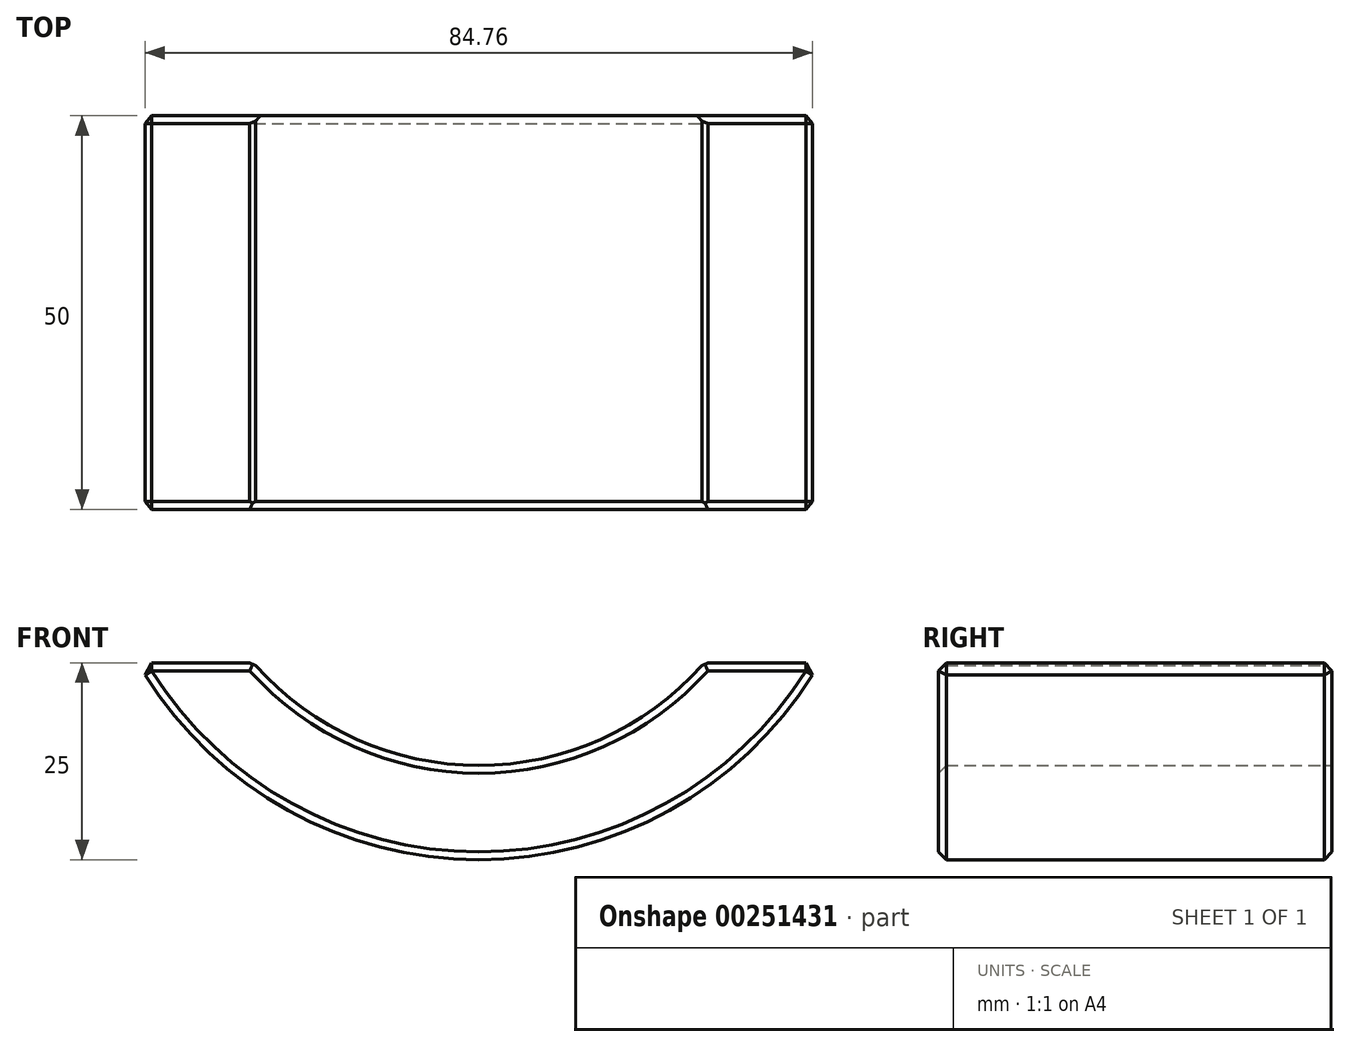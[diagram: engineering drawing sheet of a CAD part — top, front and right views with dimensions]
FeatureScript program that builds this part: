
annotation { "Feature Type Name" : "Feature", "Feature Type Description" : "" }
export const myFeature = defineFeature(function(context is Context, id is Id, definition is map)
    precondition{}
    {
        {
            var Q0;
            Q0=qCreatedBy(makeId("Front.planeOp"),FACE);
            var sketch = newSketch(context, id + "F0", { "sketchPlane" : qUnion([Q0])});
            skCircle(sketch, "E0", {"center": v(0, 0) * mm, "radius": 50 * mm});
            skLineSegment(sketch, "E1", {"start": v(-55.86, -25) * mm, "end": v(60.42, -25) * mm});
            skSolve(sketch);
        }
        {
            var Q0;
            {var subQ0=sQuery(id+"F0.wireOp",EDGE,"E1");var subQ1=sQuery(id+"F0.wireOp",EDGE,"E0");var subQ2=makeQuery(id+"F0.imprint","INTERSECT",VERTEX,{"disambiguationData":[OD(0.0)],"derivedFrom":[subQ1,subQ0]});Q0=makeQuery(id+"F0.imprint","IMPRINT",FACE,{"disambiguationData":[TD([[makeQuery(id+"F0.imprint","IMPRINT",EDGE,{"disambiguationData":[TD([[subQ2,1.0]])],"derivedFrom":subQ1}),1.0]])]});}
            extrude(context, id + "F1", {"entities" : qUnion([Q0]), "depth" : 50 * mm});
        }
        {
            var Q0;
            {var subQ0=sQuery(id+"F0.wireOp",EDGE,"E1");var subQ1=sQuery(id+"F0.wireOp",EDGE,"E0");Q0=makeQuery(id+"F1.opExtrude","SWEPT_EDGE",EDGE,{"disambiguationData":[OSD([subQ1,subQ0]),TDD([makeQuery(id+"F0.imprint","INTERSECT",VERTEX,{"disambiguationData":[OD(1.0)],"derivedFrom":[subQ1,subQ0]})])]});}
            cPlane(context, id + "F2", {"entities" : qUnion([Q0]), "cplaneType" : CPlaneType.LINE_ANGLE, "offset" : 25 * mm, "angle" : 90 * degree, "width" : 150 * mm, "height" : 150 * mm});
        }
        {
            var Q0;
            Q0=qCreatedBy(id+"F2.planeOp",FACE);
            var sketch = newSketch(context, id + "F3", { "sketchPlane" : qUnion([Q0])});
            skLineSegment(sketch, "E2.bottom", {"start": v(-42.5, 50.98) * mm, "end": v(-7.5, 50.98) * mm});
            skLineSegment(sketch, "E2.top", {"start": v(-42.5, -15) * mm, "end": v(-7.5, -15) * mm});
            skLineSegment(sketch, "E2.left", {"start": v(-42.5, 50.98) * mm, "end": v(-42.5, -15) * mm});
            skLineSegment(sketch, "E2.right", {"start": v(-7.5, 50.98) * mm, "end": v(-7.5, -15) * mm});
            skLineSegment(sketch, "E3", {"start": v(-50, 50) * mm, "end": v(0, 50) * mm});
            skLineSegment(sketch, "E4", {"start": v(-50, 50) * mm, "end": v(0, 50) * mm, "construction": true});
            skSolve(sketch);
        }
        {
            var Q0;
            Q0 = qSketchRegion(id + "F3", true);
            extrude(context, id + "F4", {"entities" : qUnion([Q0]), "operationType" : NewBodyOperationType.REMOVE, "oppositeDirection" : true, "depth" : 123.6 * mm, "hasSecondDirection" : true, "secondDirectionOppositeDirection" : false, "secondDirectionDepth" : 25 * mm});
        }
        {
            var Q0;
            Q0=makeQuery(id+"F1.opExtrude","CAP_EDGE",EDGE,{"disambiguationData":[OSD([sQuery(id+"F0.wireOp",EDGE,"E0")])],"isStart":true});
            var Q1;
            Q1=makeQuery(id+"F4.boolean.opBoolean","INTERSECT",EDGE,{"derivedFrom":[makeQuery(id+"F1.opExtrude","SWEPT_FACE",FACE,{"disambiguationData":[OSD([sQuery(id+"F0.wireOp",EDGE,"E0")])]}),makeQuery(id+"F4.opExtrude","SWEPT_FACE",FACE,{"disambiguationData":[OSD([sQuery(id+"F3.wireOp",EDGE,"E2.right")])]})]});
            var Q2;
            Q2=makeQuery(id+"F4.boolean.opBoolean","INTERSECT",EDGE,{"derivedFrom":[makeQuery(id+"F1.opExtrude","SWEPT_FACE",FACE,{"disambiguationData":[OSD([sQuery(id+"F0.wireOp",EDGE,"E0")])]}),makeQuery(id+"F4.opExtrude","SWEPT_FACE",FACE,{"disambiguationData":[OSD([sQuery(id+"F3.wireOp",EDGE,"E2.left")])]})]});
            var Q3;
            Q3=makeQuery(id+"F1.opExtrude","CAP_EDGE",EDGE,{"disambiguationData":[OSD([sQuery(id+"F0.wireOp",EDGE,"E0")])],"isStart":false});
            var Q4;
            Q4=makeQuery(id+"F4.boolean.opBoolean","INTERSECT",EDGE,{"disambiguationData":[OD(1.0)],"derivedFrom":[makeQuery(id+"F1.opExtrude","SWEPT_FACE",FACE,{"disambiguationData":[OSD([sQuery(id+"F0.wireOp",EDGE,"E0")])]}),makeQuery(id+"F4.opExtrude","SWEPT_FACE",FACE,{"disambiguationData":[OSD([sQuery(id+"F3.wireOp",EDGE,"E2.top")])]})]});
            var Q5;
            {var subQ0=sQuery(id+"F0.wireOp",EDGE,"E1");var subQ1=sQuery(id+"F0.wireOp",EDGE,"E0");Q5=makeQuery(id+"F1.opExtrude","SWEPT_EDGE",EDGE,{"disambiguationData":[OSD([subQ1,subQ0]),TDD([makeQuery(id+"F0.imprint","INTERSECT",VERTEX,{"disambiguationData":[OD(1.0)],"derivedFrom":[subQ1,subQ0]})])]});}
            var Q6;
            Q6=makeQuery(id+"F1.opExtrude","CAP_EDGE",EDGE,{"disambiguationData":[OSD([sQuery(id+"F0.wireOp",EDGE,"E1")])],"isStart":true});
            var Q7;
            Q7=makeQuery(id+"F4.boolean.opBoolean","INTERSECT",EDGE,{"disambiguationData":[OD(0.0)],"derivedFrom":[makeQuery(id+"F1.opExtrude","SWEPT_FACE",FACE,{"disambiguationData":[OSD([sQuery(id+"F0.wireOp",EDGE,"E0")])]}),makeQuery(id+"F4.opExtrude","SWEPT_FACE",FACE,{"disambiguationData":[OSD([sQuery(id+"F3.wireOp",EDGE,"E2.top")])]})]});
            var Q8;
            {var subQ0=sQuery(id+"F0.wireOp",EDGE,"E1");var subQ1=sQuery(id+"F0.wireOp",EDGE,"E0");Q8=makeQuery(id+"F1.opExtrude","SWEPT_EDGE",EDGE,{"disambiguationData":[OSD([subQ1,subQ0]),TDD([makeQuery(id+"F0.imprint","INTERSECT",VERTEX,{"disambiguationData":[OD(0.0)],"derivedFrom":[subQ1,subQ0]})])]});}
            var Q9;
            Q9=makeQuery(id+"F1.opExtrude","CAP_EDGE",EDGE,{"disambiguationData":[OSD([sQuery(id+"F0.wireOp",EDGE,"E1")])],"isStart":false});
            chamfer(context, id + "F5", {"entities" : qUnion([Q0, Q1, Q2, Q3, Q4, Q5, Q6, Q7, Q8, Q9]), "width" : 1 * mm, "tangentPropagation" : true});
        }
        {
            var Q0;
            Q0=qCreatedBy(makeId("Front.planeOp"),FACE);
            var sketch = newSketch(context, id + "F6", { "sketchPlane" : qUnion([Q0])});
            skCircle(sketch, "E5", {"center": v(0, 0) * mm, "radius": 38.02 * mm});
            skSolve(sketch);
        }
        {
            var Q0;
            Q0 = qSketchRegion(id + "F6", true);
            extrude(context, id + "F7", {"entities" : qUnion([Q0]), "operationType" : NewBodyOperationType.REMOVE, "depth" : 97.2 * mm});
        }
        {
            var Q0;
            Q0=makeQuery(id+"F7.boolean.opBoolean","INTERSECT",EDGE,{"disambiguationData":[OD(0.0)],"derivedFrom":[makeQuery(id+"F1.opExtrude","SWEPT_FACE",FACE,{"disambiguationData":[OSD([sQuery(id+"F0.wireOp",EDGE,"E1")])]}),makeQuery(id+"F7.opExtrude","SWEPT_FACE",FACE,{"disambiguationData":[OSD([sQuery(id+"F6.wireOp",EDGE,"E5")])]})]});
            var Q1;
            Q1=makeQuery(id+"F7.boolean.opBoolean","COPY",EDGE,{"derivedFrom":makeQuery(id+"F7.opExtrude","CAP_EDGE",EDGE,{"disambiguationData":[OSD([sQuery(id+"F6.wireOp",EDGE,"E5")])],"isStart":true})});
            var Q2;
            Q2=makeQuery(id+"F7.boolean.opBoolean","INTERSECT",EDGE,{"derivedFrom":[makeQuery(id+"F1.opExtrude","CAP_FACE",FACE,{"disambiguationData":[OSD([sQuery(id+"F0.wireOp",EDGE,"E0"),sQuery(id+"F0.wireOp",EDGE,"E1")])],"isStart":false}),makeQuery(id+"F7.opExtrude","SWEPT_FACE",FACE,{"disambiguationData":[OSD([sQuery(id+"F6.wireOp",EDGE,"E5")])]})]});
            var Q3;
            Q3=makeQuery(id+"F7.boolean.opBoolean","INTERSECT",EDGE,{"disambiguationData":[OD(1.0)],"derivedFrom":[makeQuery(id+"F1.opExtrude","SWEPT_FACE",FACE,{"disambiguationData":[OSD([sQuery(id+"F0.wireOp",EDGE,"E1")])]}),makeQuery(id+"F7.opExtrude","SWEPT_FACE",FACE,{"disambiguationData":[OSD([sQuery(id+"F6.wireOp",EDGE,"E5")])]})]});
            var Q4;
            Q4=makeQuery(id+"F7.boolean.opBoolean","INTERSECT",EDGE,{"disambiguationData":[OD(1.0)],"derivedFrom":[makeQuery(id+"F4.boolean.opBoolean","COPY",FACE,{"derivedFrom":makeQuery(id+"F4.opExtrude","SWEPT_FACE",FACE,{"disambiguationData":[OSD([sQuery(id+"F3.wireOp",EDGE,"E2.top")])]})}),makeQuery(id+"F7.opExtrude","SWEPT_FACE",FACE,{"disambiguationData":[OSD([sQuery(id+"F6.wireOp",EDGE,"E5")])]})]});
            var Q5;
            Q5=makeQuery(id+"F7.boolean.opBoolean","INTERSECT",EDGE,{"derivedFrom":[makeQuery(id+"F4.boolean.opBoolean","COPY",FACE,{"derivedFrom":makeQuery(id+"F4.opExtrude","SWEPT_FACE",FACE,{"disambiguationData":[OSD([sQuery(id+"F3.wireOp",EDGE,"E2.left")])]})}),makeQuery(id+"F7.opExtrude","SWEPT_FACE",FACE,{"disambiguationData":[OSD([sQuery(id+"F6.wireOp",EDGE,"E5")])]})]});
            var Q6;
            Q6=makeQuery(id+"F7.boolean.opBoolean","INTERSECT",EDGE,{"derivedFrom":[makeQuery(id+"F4.boolean.opBoolean","COPY",FACE,{"derivedFrom":makeQuery(id+"F4.opExtrude","SWEPT_FACE",FACE,{"disambiguationData":[OSD([sQuery(id+"F3.wireOp",EDGE,"E2.right")])]})}),makeQuery(id+"F7.opExtrude","SWEPT_FACE",FACE,{"disambiguationData":[OSD([sQuery(id+"F6.wireOp",EDGE,"E5")])]})]});
            var Q7;
            Q7=makeQuery(id+"F7.boolean.opBoolean","INTERSECT",EDGE,{"disambiguationData":[OD(0.0)],"derivedFrom":[makeQuery(id+"F4.boolean.opBoolean","COPY",FACE,{"derivedFrom":makeQuery(id+"F4.opExtrude","SWEPT_FACE",FACE,{"disambiguationData":[OSD([sQuery(id+"F3.wireOp",EDGE,"E2.top")])]})}),makeQuery(id+"F7.opExtrude","SWEPT_FACE",FACE,{"disambiguationData":[OSD([sQuery(id+"F6.wireOp",EDGE,"E5")])]})]});
            chamfer(context, id + "F8", {"entities" : qUnion([Q0, Q1, Q2, Q3, Q4, Q5, Q6, Q7]), "width" : 1 * mm, "tangentPropagation" : true});
        }
    });
